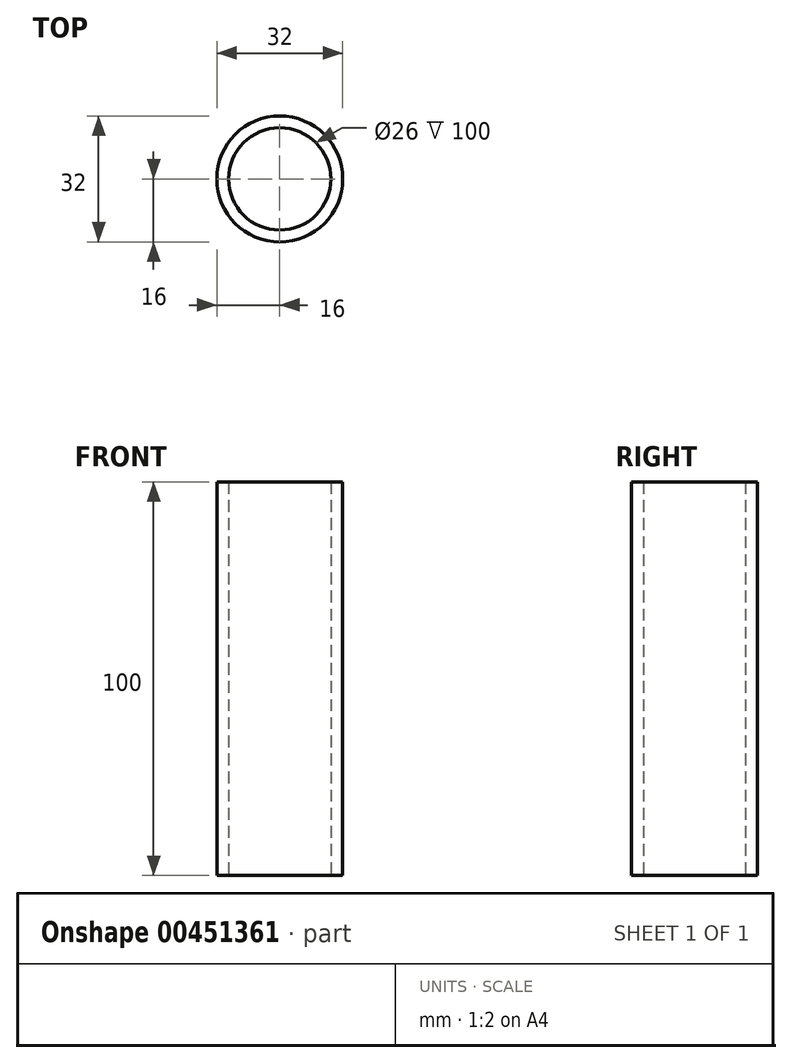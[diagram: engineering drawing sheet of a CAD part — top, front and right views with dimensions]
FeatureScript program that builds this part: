
annotation { "Feature Type Name" : "Feature", "Feature Type Description" : "" }
export const myFeature = defineFeature(function(context is Context, id is Id, definition is map)
    precondition{}
    {
        {
            var Q0;
            Q0=qCreatedBy(makeId("Top.planeOp"),FACE);
            var sketch = newSketch(context, id + "F0", { "sketchPlane" : qUnion([Q0])});
            skCircle(sketch, "E0", {"center": v(0, 0) * mm, "radius": 16 * mm});
            skCircle(sketch, "E1", {"center": v(0, 0) * mm, "radius": 13 * mm});
            skSolve(sketch);
        }
        {
            var Q0;
            Q0 = qSketchRegion(id + "F0", true);
            extrude(context, id + "F1", {"entities" : qUnion([Q0]), "depth" : 100 * mm});
        }
    });
